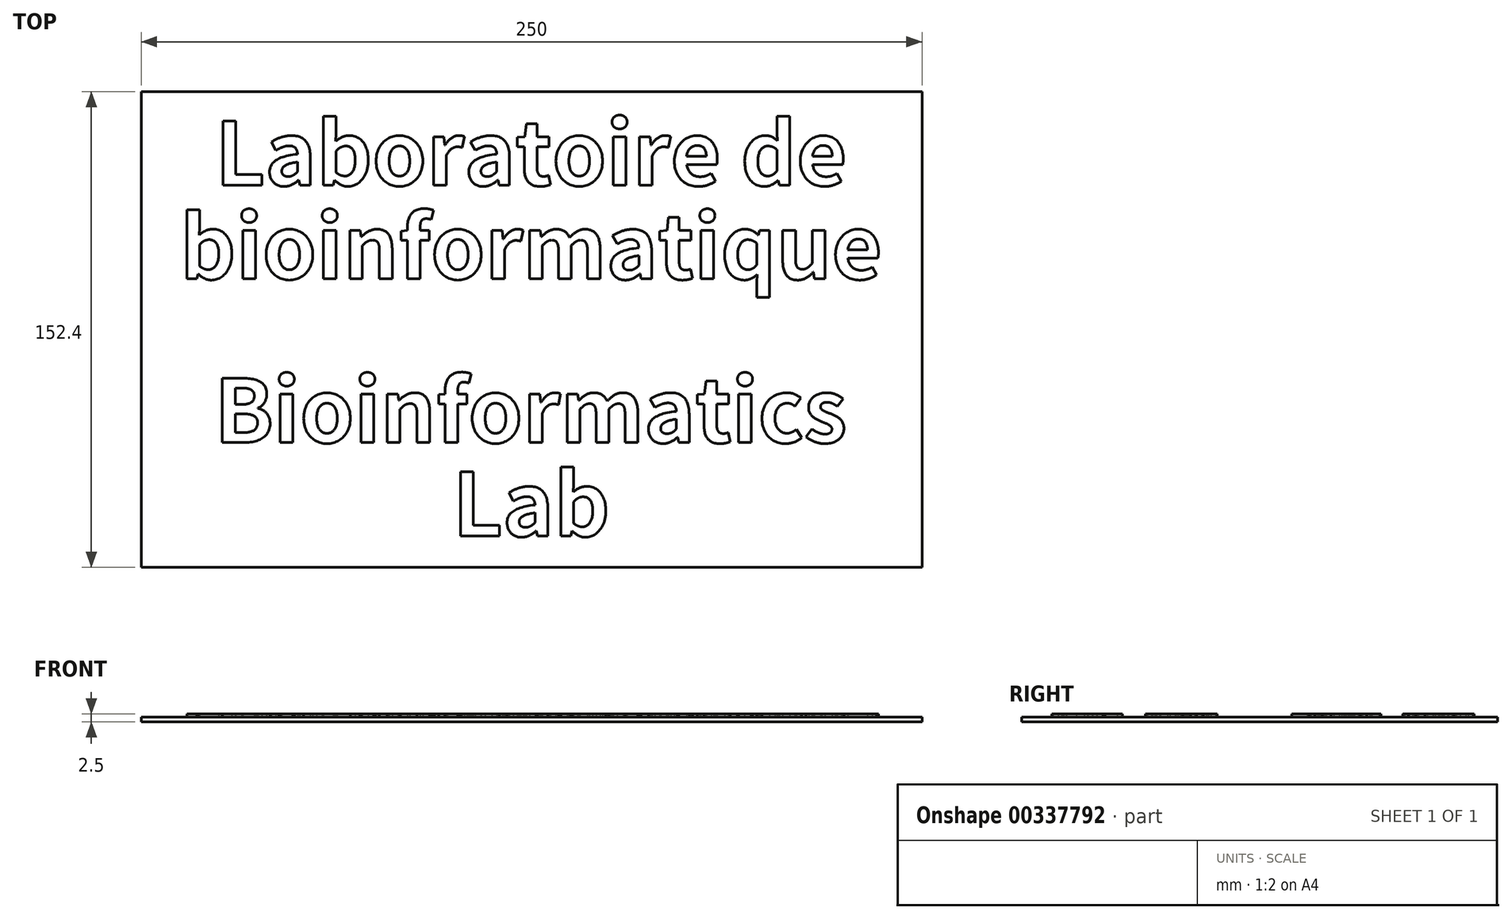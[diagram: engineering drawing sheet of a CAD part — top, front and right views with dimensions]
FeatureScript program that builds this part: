
annotation { "Feature Type Name" : "Feature", "Feature Type Description" : "" }
export const myFeature = defineFeature(function(context is Context, id is Id, definition is map)
    precondition{}
    {
        {
            var Q0;
            Q0=qCreatedBy(makeId("Top.planeOp"),FACE);
            var sketch = newSketch(context, id + "F0", { "sketchPlane" : qUnion([Q0])});
            skLineSegment(sketch, "E0.bottom", {"start": v(125, -76.2) * mm, "end": v(-125, -76.2) * mm});
            skLineSegment(sketch, "E0.top", {"start": v(125, 76.2) * mm, "end": v(-125, 76.2) * mm});
            skLineSegment(sketch, "E0.left", {"start": v(125, -76.2) * mm, "end": v(125, 76.2) * mm});
            skLineSegment(sketch, "E0.right", {"start": v(-125, -76.2) * mm, "end": v(-125, 76.2) * mm});
            skPoint(sketch, "E0.middle", {"position": v(0, 0) * mm});
            skSolve(sketch);
        }
        {
            var Q0;
            Q0=qSketchRegion(id+"F0",true);
            extrude(context, id + "F1", {"entities" : qUnion([Q0]), "depth" : 1.5 * mm});
        }
        {
            var Q0;
            Q0=makeQuery(id+"F1.opExtrude","CAP_FACE",FACE,{"disambiguationData":[OSD([sQuery(id+"F0.wireOp",EDGE,"E0.bottom"),sQuery(id+"F0.wireOp",EDGE,"E0.top"),sQuery(id+"F0.wireOp",EDGE,"E0.left"),sQuery(id+"F0.wireOp",EDGE,"E0.right")])],"isStart":false});
            var sketch = newSketch(context, id + "F2", { "sketchPlane" : qUnion([Q0])});
            skText(sketch, "E1", { "text": "Laboratoire de", "fontName": "NotoSansCJKsc-Bold.otf"});
            skText(sketch, "E2", { "text": "Bioinformatics", "fontName": "NotoSansCJKsc-Bold.otf"});
            skText(sketch, "E3", { "text": "Lab", "fontName": "NotoSansCJKsc-Bold.otf"});
            skText(sketch, "E4", { "text": "bioinformatique", "fontName": "NotoSansCJKsc-Bold.otf"});
            const initialGuessF2  = {"E1": [-0.10137, 0.0462, 1, 0, 0.02], "E2": [-0.1016, -0.0362, 1, 0, 0.02], "E3": [-0.02531, -0.0662, 1, 0, 0.02], "E4": [-0.11262, 0.0162, 1, 0, 0.02]};
            skSetInitialGuess(sketch, initialGuessF2);
            skSolve(sketch);
        }
        {
            var Q0;
            Q0=qSketchRegion(id+"F2",true);
            extrude(context, id + "F3", {"entities" : qUnion([Q0]), "operationType" : NewBodyOperationType.ADD, "depth" : 1 * mm});
        }
    });
